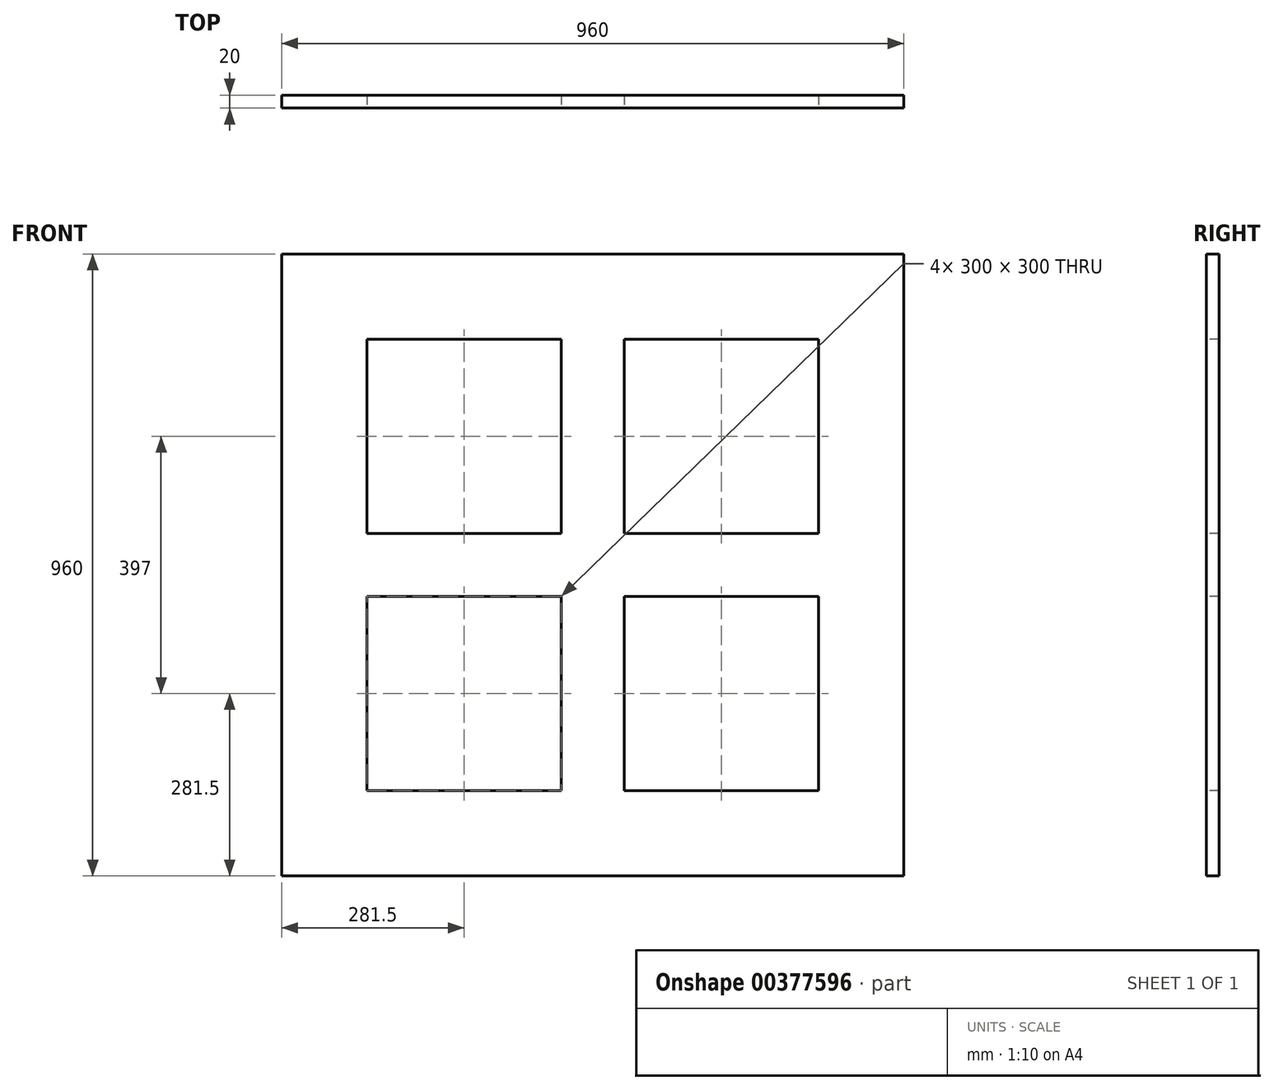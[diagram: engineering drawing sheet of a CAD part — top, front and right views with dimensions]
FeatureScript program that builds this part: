
annotation { "Feature Type Name" : "Feature", "Feature Type Description" : "" }
export const myFeature = defineFeature(function(context is Context, id is Id, definition is map)
    precondition{}
    {
        {
            var Q0;
            Q0=qCreatedBy(makeId("Front.planeOp"),FACE);
            var sketch = newSketch(context, id + "F0", { "sketchPlane" : qUnion([Q0])});
            skLineSegment(sketch, "E0.bottom", {"start": v(-480, 480) * mm, "end": v(480, 480) * mm});
            skLineSegment(sketch, "E0.top", {"start": v(-480, -480) * mm, "end": v(480, -480) * mm});
            skLineSegment(sketch, "E0.left", {"start": v(-480, 480) * mm, "end": v(-480, -480) * mm});
            skLineSegment(sketch, "E0.right", {"start": v(480, 480) * mm, "end": v(480, -480) * mm});
            skPoint(sketch, "E0.middle", {"position": v(0, 0) * mm});
            skSolve(sketch);
        }
        {
            var Q0;
            Q0 = qSketchRegion(id + "F0", true);
            extrude(context, id + "F1", {"entities" : qUnion([Q0]), "depth" : 20 * mm});
        }
        {
            var Q0;
            Q0=makeQuery(id+"F1.opExtrude","CAP_FACE",FACE,{"disambiguationData":[OSD([sQuery(id+"F0.wireOp",EDGE,"E0.bottom"),sQuery(id+"F0.wireOp",EDGE,"E0.top"),sQuery(id+"F0.wireOp",EDGE,"E0.left"),sQuery(id+"F0.wireOp",EDGE,"E0.right")])],"isStart":false});
            var sketch = newSketch(context, id + "F2", { "sketchPlane" : qUnion([Q0])});
            skLineSegment(sketch, "E1.bottom", {"start": v(-348.5, 348.5) * mm, "end": v(-48.5, 348.5) * mm});
            skLineSegment(sketch, "E1.top", {"start": v(-348.5, 48.5) * mm, "end": v(-48.5, 48.5) * mm});
            skLineSegment(sketch, "E1.left", {"start": v(-348.5, 348.5) * mm, "end": v(-348.5, 48.5) * mm});
            skLineSegment(sketch, "E1.right", {"start": v(-48.5, 348.5) * mm, "end": v(-48.5, 48.5) * mm});
            skLineSegment(sketch, "E2.bottom", {"start": v(-348.5, -48.5) * mm, "end": v(-48.5, -48.5) * mm});
            skLineSegment(sketch, "E2.top", {"start": v(-348.5, -348.5) * mm, "end": v(-48.5, -348.5) * mm});
            skLineSegment(sketch, "E2.left", {"start": v(-348.5, -48.5) * mm, "end": v(-348.5, -348.5) * mm});
            skLineSegment(sketch, "E2.right", {"start": v(-48.5, -48.5) * mm, "end": v(-48.5, -348.5) * mm});
            skLineSegment(sketch, "E3.bottom", {"start": v(48.5, 348.5) * mm, "end": v(348.5, 348.5) * mm});
            skLineSegment(sketch, "E3.top", {"start": v(48.5, 48.5) * mm, "end": v(348.5, 48.5) * mm});
            skLineSegment(sketch, "E3.left", {"start": v(48.5, 348.5) * mm, "end": v(48.5, 48.5) * mm});
            skLineSegment(sketch, "E3.right", {"start": v(348.5, 348.5) * mm, "end": v(348.5, 48.5) * mm});
            skLineSegment(sketch, "E4.bottom", {"start": v(48.5, -48.5) * mm, "end": v(348.5, -48.5) * mm});
            skLineSegment(sketch, "E4.top", {"start": v(48.5, -348.5) * mm, "end": v(348.5, -348.5) * mm});
            skLineSegment(sketch, "E4.left", {"start": v(48.5, -48.5) * mm, "end": v(48.5, -348.5) * mm});
            skLineSegment(sketch, "E4.right", {"start": v(348.5, -48.5) * mm, "end": v(348.5, -348.5) * mm});
            skLineSegment(sketch, "E5", {"start": v(-48.5, 48.5) * mm, "end": v(48.5, -48.5) * mm, "construction": true});
            skLineSegment(sketch, "E6", {"start": v(48.5, 48.5) * mm, "end": v(-48.5, -48.5) * mm, "construction": true});
            skPoint(sketch, "E7", {"position": v(0, 0) * mm});
            skLineSegment(sketch, "E8", {"start": v(-348.5, 348.5) * mm, "end": v(-348.5, 480) * mm, "construction": true});
            skLineSegment(sketch, "E9", {"start": v(-348.5, 348.5) * mm, "end": v(-480, 348.5) * mm, "construction": true});
            skLineSegment(sketch, "E10", {"start": v(-48.5, 48.5) * mm, "end": v(48.5, 48.5) * mm, "construction": true});
            skLineSegment(sketch, "E11", {"start": v(-48.5, 48.5) * mm, "end": v(-48.5, -48.5) * mm, "construction": true});
            skSolve(sketch);
        }
        {
            var Q0;
            Q0=makeQuery(id+"F2.imprint","IMPRINT",FACE,{"disambiguationData":[TD([[makeQuery(id+"F2.imprint","IMPRINT",EDGE,{"derivedFrom":sQuery(id+"F2.wireOp",EDGE,"E2.bottom")}),-1.0]])]});
            var Q1;
            Q1=makeQuery(id+"F2.imprint","IMPRINT",FACE,{"disambiguationData":[TD([[makeQuery(id+"F2.imprint","IMPRINT",EDGE,{"derivedFrom":sQuery(id+"F2.wireOp",EDGE,"E3.bottom")}),-1.0]])]});
            var Q2;
            Q2=makeQuery(id+"F2.imprint","IMPRINT",FACE,{"disambiguationData":[TD([[makeQuery(id+"F2.imprint","IMPRINT",EDGE,{"derivedFrom":sQuery(id+"F2.wireOp",EDGE,"E4.bottom")}),-1.0]])]});
            var Q3;
            Q3=makeQuery(id+"F2.imprint","IMPRINT",FACE,{"disambiguationData":[TD([[makeQuery(id+"F2.imprint","IMPRINT",EDGE,{"derivedFrom":sQuery(id+"F2.wireOp",EDGE,"E1.bottom")}),-1.0]])]});
            extrude(context, id + "F3", {"entities" : qUnion([Q0, Q1, Q2, Q3]), "operationType" : NewBodyOperationType.REMOVE, "endBound" : BoundingType.THROUGH_ALL, "oppositeDirection" : true, "depth" : 25 * mm});
        }
    });
